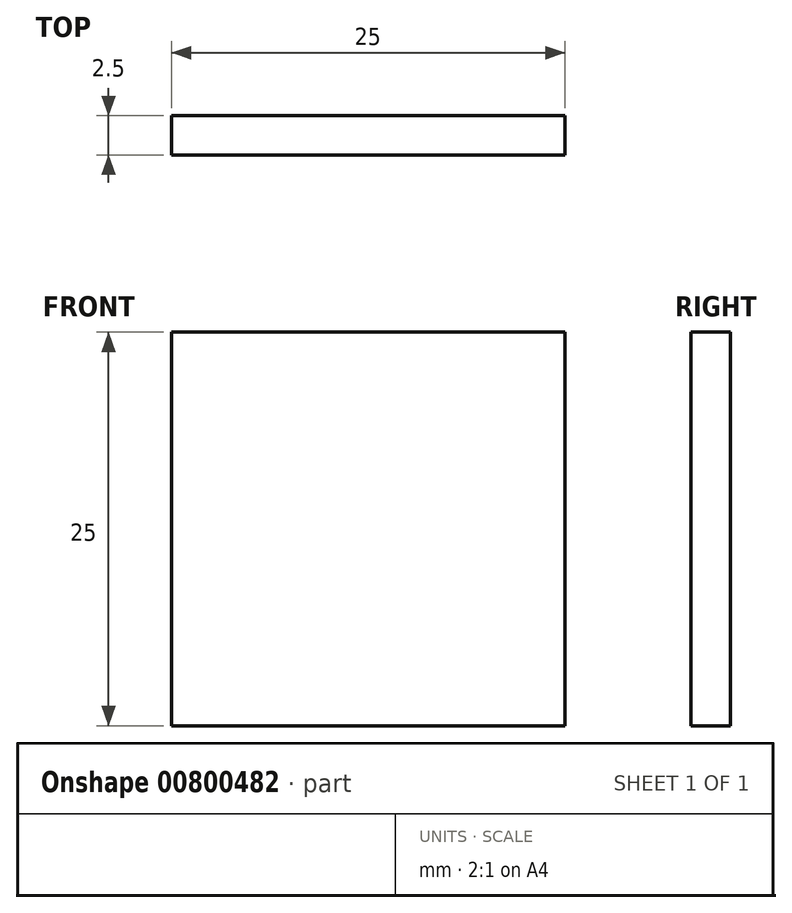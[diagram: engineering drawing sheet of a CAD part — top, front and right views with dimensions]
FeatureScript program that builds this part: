
annotation { "Feature Type Name" : "Feature", "Feature Type Description" : "" }
export const myFeature = defineFeature(function(context is Context, id is Id, definition is map)
    precondition{}
    {
        {
            var Q0;
            Q0=qCreatedBy(makeId("Front.planeOp"),FACE);
            var sketch = newSketch(context, id + "F0", { "sketchPlane" : qUnion([Q0])});
            skLineSegment(sketch, "E0.bottom", {"start": v(-12.5, 12.5) * mm, "end": v(12.5, 12.5) * mm});
            skLineSegment(sketch, "E0.top", {"start": v(-12.5, -12.5) * mm, "end": v(12.5, -12.5) * mm});
            skLineSegment(sketch, "E0.left", {"start": v(-12.5, 12.5) * mm, "end": v(-12.5, -12.5) * mm});
            skLineSegment(sketch, "E0.right", {"start": v(12.5, 12.5) * mm, "end": v(12.5, -12.5) * mm});
            skPoint(sketch, "E0.middle", {"position": v(0, 0) * mm});
            skSolve(sketch);
        }
        {
            var Q0;
            Q0=makeQuery(id+"F0.imprint","IMPRINT",FACE,{"disambiguationData":[TD([[makeQuery(id+"F0.imprint","IMPRINT",EDGE,{"derivedFrom":sQuery(id+"F0.wireOp",EDGE,"E0.bottom")}),-1.0]])]});
            extrude(context, id + "F1", {"entities" : qUnion([Q0]), "depth" : 2.5 * mm, "offsetDistance" : 25 * mm});
        }
    });
